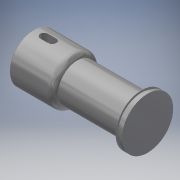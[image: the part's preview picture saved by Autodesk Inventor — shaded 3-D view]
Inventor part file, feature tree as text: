
AUTODESK INVENTOR PART (.ipt)
format: ipt  version: 2019 (Build 230136000, 136)  size: 175,616 bytes
history: native  units: mm
features: other x8, chamfer x1, fillet x1
ambient origin geometry x6: Origin, XZ Plane, XY Plane, X Axis, Y Axis, Z Axis
bodies: Body1 (feature_tree)
feature tree (10):
  other  "實體1"
  other  "迴轉1"
  chamfer  "倒角1"  [1 undecoded]
  fillet  "圓角1"  Radius=15.0mm
  other  "鍵槽1"
  other  "扣環槽1"
  other  "起始平面"
  other  "主要草圖"
  other  "iFeature3:1"
  other  "iFeature27:1"
note: 1 required parameter value undecoded (feature->parameter linkage not recoverable at this tier; creation-order binding heuristic only, values carry confidence <= 0.55)
